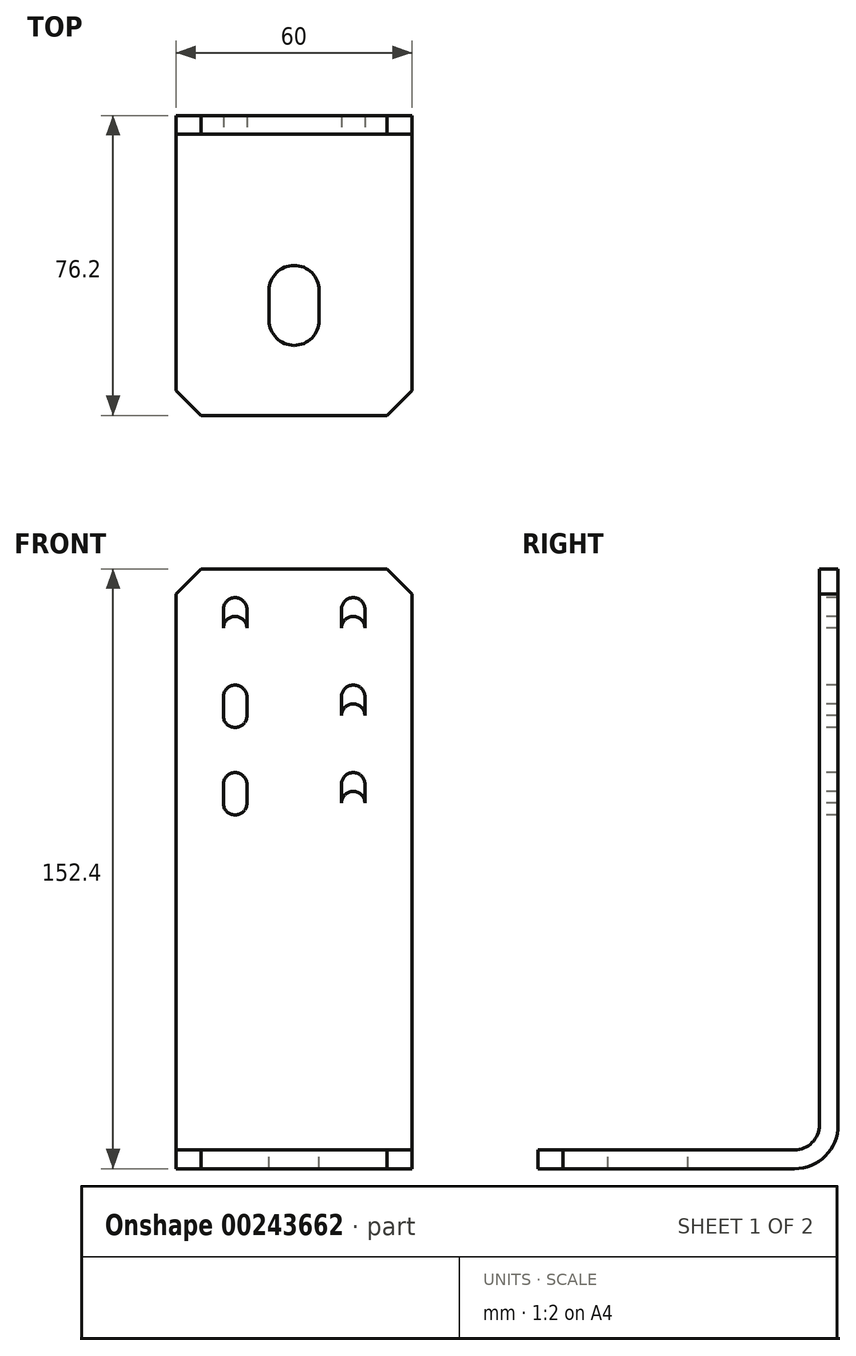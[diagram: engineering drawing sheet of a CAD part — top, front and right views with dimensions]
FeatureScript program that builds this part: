
annotation { "Feature Type Name" : "Feature", "Feature Type Description" : "" }
export const myFeature = defineFeature(function(context is Context, id is Id, definition is map)
    precondition{}
    {
        {
            var Q0;
            Q0=qCreatedBy(makeId("Right.planeOp"),FACE);
            var sketch = newSketch(context, id + "F0", { "sketchPlane" : qUnion([Q0])});
            skLineSegment(sketch, "E0", {"start": v(0, 0) * mm, "end": v(0, 150.02) * mm, "construction": true});
            skLineSegment(sketch, "E1", {"start": v(0, 0) * mm, "end": v(-73.82, 0) * mm, "construction": true});
            skLineSegment(sketch, "E2", {"start": v(-73.82, 2.38) * mm, "end": v(-73.82, -2.38) * mm});
            skLineSegment(sketch, "E3", {"start": v(-73.82, -2.38) * mm, "end": v(2.38, -2.38) * mm});
            skLineSegment(sketch, "E4", {"start": v(2.38, -2.38) * mm, "end": v(2.38, 150.02) * mm});
            skLineSegment(sketch, "E5", {"start": v(2.38, 150.02) * mm, "end": v(-2.38, 150.02) * mm});
            skLineSegment(sketch, "E6", {"start": v(-2.38, 150.02) * mm, "end": v(-2.38, 2.38) * mm});
            skLineSegment(sketch, "E7", {"start": v(-2.38, 2.38) * mm, "end": v(-73.82, 2.38) * mm});
            skSolve(sketch);
        }
        {
            var Q0;
            Q0 = qSketchRegion(id + "F0", true);
            extrude(context, id + "F1", {"entities" : qUnion([Q0]), "endBound" : BoundingType.SYMMETRIC, "depth" : 60 * mm});
        }
        {
            var Q0;
            Q0=makeQuery(id+"F1.opExtrude","SWEPT_EDGE",EDGE,{"disambiguationData":[OSD([sQuery(id+"F0.wireOp",EDGE,"E6"),sQuery(id+"F0.wireOp",EDGE,"E7")])]});
            fillet(context, id + "F2", {"entities" : qUnion([Q0]), "radius" : 6.35 * mm, "tangentPropagation" : true, "allowEdgeOverflow" : false});
        }
        {
            var Q0;
            Q0=makeQuery(id+"F1.opExtrude","SWEPT_EDGE",EDGE,{"disambiguationData":[OSD([sQuery(id+"F0.wireOp",EDGE,"E3"),sQuery(id+"F0.wireOp",EDGE,"E4")])]});
            fillet(context, id + "F3", {"entities" : qUnion([Q0]), "radius" : 11.1 * mm, "tangentPropagation" : true, "allowEdgeOverflow" : false});
        }
        {
            var Q0;
            Q0=makeQuery(id+"F1.opExtrude","CAP_EDGE",EDGE,{"disambiguationData":[OSD([sQuery(id+"F0.wireOp",EDGE,"E5")])],"isStart":false});
            var Q1;
            Q1=makeQuery(id+"F1.opExtrude","CAP_EDGE",EDGE,{"disambiguationData":[OSD([sQuery(id+"F0.wireOp",EDGE,"E5")])],"isStart":true});
            var Q2;
            Q2=makeQuery(id+"F1.opExtrude","CAP_EDGE",EDGE,{"disambiguationData":[OSD([sQuery(id+"F0.wireOp",EDGE,"E2")])],"isStart":true});
            var Q3;
            Q3=makeQuery(id+"F1.opExtrude","CAP_EDGE",EDGE,{"disambiguationData":[OSD([sQuery(id+"F0.wireOp",EDGE,"E2")])],"isStart":false});
            chamfer(context, id + "F4", {"entities" : qUnion([Q0, Q1, Q2, Q3]), "width" : 6.35 * mm, "tangentPropagation" : true});
        }
        {
            var Q0;
            Q0=makeQuery(id+"F1.opExtrude","SWEPT_FACE",FACE,{"disambiguationData":[OSD([sQuery(id+"F0.wireOp",EDGE,"E7")])]});
            var sketch = newSketch(context, id + "F5", { "sketchPlane" : qUnion([Q0])});
            skLineSegment(sketch, "E8", {"start": v(0, 2.38) * mm, "end": v(0, -42.07) * mm, "construction": true});
            skCircle(sketch, "E9", {"center": v(0, -42.07) * mm, "radius": 6.35 * mm});
            skCircle(sketch, "E10", {"center": v(0, -49.69) * mm, "radius": 6.35 * mm});
            skLineSegment(sketch, "E11", {"start": v(0, -42.07) * mm, "end": v(0, -49.69) * mm, "construction": true});
            skLineSegment(sketch, "E12", {"start": v(6.35, -42.07) * mm, "end": v(6.35, -49.69) * mm});
            skLineSegment(sketch, "E13", {"start": v(-6.35, -42.07) * mm, "end": v(-6.35, -49.69) * mm});
            skSolve(sketch);
        }
        {
            var Q0;
            Q0 = qSketchRegion(id + "F5", true);
            extrude(context, id + "F6", {"entities" : qUnion([Q0]), "operationType" : NewBodyOperationType.REMOVE, "endBound" : BoundingType.THROUGH_ALL, "oppositeDirection" : true, "depth" : 25.4 * mm});
        }
        {
            var Q0;
            Q0 = qSketchRegion(id + "F5", true);
            var Q1;
            {var subQ0=sQuery(id+"F5.wireOp",EDGE,"E10");var subQ1=sQuery(id+"F5.wireOp",EDGE,"E9");var subQ2=makeQuery(id+"F5.imprint","INTERSECT",VERTEX,{"disambiguationData":[OD(0.0)],"derivedFrom":[subQ1,subQ0]});Q1=makeQuery(id+"F6.boolean.opBoolean","SPLIT",FACE,{"disambiguationData":[TD([makeQuery(id+"F6.opExtrude","SWEPT_FACE",FACE,{"disambiguationData":[OSD([subQ1]),TDD([makeQuery(id+"F5.imprint","IMPRINT",EDGE,{"disambiguationData":[TD([[subQ2,-1.0]])],"derivedFrom":subQ1})])]})])],"derivedFrom":makeQuery(id+"F1.opExtrude","SWEPT_FACE",FACE,{"disambiguationData":[OSD([sQuery(id+"F0.wireOp",EDGE,"E7")])]})});}
            extrude(context, id + "F7", {"entities" : qUnion([Q0, Q1]), "operationType" : NewBodyOperationType.REMOVE, "endBound" : BoundingType.THROUGH_ALL, "oppositeDirection" : true, "depth" : 25.4 * mm});
        }
        {
            var Q0;
            Q0=makeQuery(id+"F1.opExtrude","SWEPT_FACE",FACE,{"disambiguationData":[OSD([sQuery(id+"F0.wireOp",EDGE,"E6")])]});
            var sketch = newSketch(context, id + "F8", { "sketchPlane" : qUnion([Q0])});
            skLineSegment(sketch, "E14", {"start": v(0, 0) * mm, "end": v(0, 150.02) * mm, "construction": true});
            skCircle(sketch, "E15", {"center": v(-15, 139.7) * mm, "radius": 3 * mm});
            skLineSegment(sketch, "E16", {"start": v(-15, 139.7) * mm, "end": v(-15, 134.94) * mm, "construction": true});
            skCircle(sketch, "E17", {"center": v(-15, 134.94) * mm, "radius": 3 * mm});
            skLineSegment(sketch, "E18", {"start": v(-12, 139.7) * mm, "end": v(-12, 134.94) * mm});
            skLineSegment(sketch, "E19", {"start": v(-18, 139.7) * mm, "end": v(-18, 134.94) * mm});
            skLineSegment(sketch, "E20", {"start": v(-18, 137.32) * mm, "end": v(-12, 137.32) * mm, "construction": true});
            skCircle(sketch, "E21.0.1.0", {"center": v(-15, 112.71) * mm, "radius": 3 * mm});
            skLineSegment(sketch, "E21.0.1.1", {"start": v(-15, 117.48) * mm, "end": v(-15, 112.71) * mm, "construction": true});
            skLineSegment(sketch, "E21.0.1.2", {"start": v(-12, 117.48) * mm, "end": v(-12, 112.71) * mm});
            skLineSegment(sketch, "E21.0.1.3", {"start": v(-18, 117.48) * mm, "end": v(-18, 112.71) * mm});
            skLineSegment(sketch, "E21.0.1.4", {"start": v(-18, 115.1) * mm, "end": v(-12, 115.1) * mm, "construction": true});
            skCircle(sketch, "E21.0.1.5", {"center": v(-15, 117.48) * mm, "radius": 3 * mm});
            skCircle(sketch, "E21.0.2.0", {"center": v(-15, 90.49) * mm, "radius": 3 * mm});
            skLineSegment(sketch, "E21.0.2.1", {"start": v(-15, 95.25) * mm, "end": v(-15, 90.49) * mm, "construction": true});
            skLineSegment(sketch, "E21.0.2.2", {"start": v(-12, 95.25) * mm, "end": v(-12, 90.49) * mm});
            skLineSegment(sketch, "E21.0.2.3", {"start": v(-18, 95.25) * mm, "end": v(-18, 90.49) * mm});
            skLineSegment(sketch, "E21.0.2.4", {"start": v(-18, 92.87) * mm, "end": v(-12, 92.87) * mm, "construction": true});
            skCircle(sketch, "E21.0.2.5", {"center": v(-15, 95.25) * mm, "radius": 3 * mm});
            skLineSegment(sketch, "E21.direction1", {"start": v(-18, 134.94) * mm, "end": v(7.6, 134.94) * mm, "construction": true});
            skLineSegment(sketch, "E21.direction2", {"start": v(-18, 134.94) * mm, "end": v(-18, 112.71) * mm, "construction": true});
            skLineSegment(sketch, "E22.MirrorCS", {"start": v(15, 139.7) * mm, "end": v(15, 134.94) * mm, "construction": true});
            skLineSegment(sketch, "E23.MirrorCS", {"start": v(15, 117.48) * mm, "end": v(15, 112.71) * mm, "construction": true});
            skLineSegment(sketch, "E24.MirrorCS", {"start": v(12, 95.25) * mm, "end": v(12, 90.49) * mm});
            skLineSegment(sketch, "E25.MirrorCS", {"start": v(18, 95.25) * mm, "end": v(18, 90.49) * mm});
            skLineSegment(sketch, "E26.MirrorCS", {"start": v(18, 92.87) * mm, "end": v(12, 92.87) * mm, "construction": true});
            skLineSegment(sketch, "E27.MirrorCS", {"start": v(18, 115.1) * mm, "end": v(12, 115.1) * mm, "construction": true});
            skLineSegment(sketch, "E28.MirrorCS", {"start": v(18, 117.48) * mm, "end": v(18, 112.71) * mm});
            skLineSegment(sketch, "E29.MirrorCS", {"start": v(12, 139.7) * mm, "end": v(12, 134.94) * mm});
            skLineSegment(sketch, "E30.MirrorCS", {"start": v(18, 139.7) * mm, "end": v(18, 134.94) * mm});
            skLineSegment(sketch, "E31.MirrorCS", {"start": v(18, 137.32) * mm, "end": v(12, 137.32) * mm, "construction": true});
            skLineSegment(sketch, "E32.MirrorCS", {"start": v(12, 117.48) * mm, "end": v(12, 112.71) * mm});
            skCircle(sketch, "E33.MirrorC", {"center": v(15, 139.7) * mm, "radius": 3 * mm});
            skCircle(sketch, "E34.MirrorC", {"center": v(15, 95.25) * mm, "radius": 3 * mm});
            skLineSegment(sketch, "E35.MirrorCS", {"start": v(15, 95.25) * mm, "end": v(15, 90.49) * mm, "construction": true});
            skLineSegment(sketch, "E36.MirrorCS", {"start": v(18, 134.94) * mm, "end": v(18, 112.71) * mm, "construction": true});
            skCircle(sketch, "E37.MirrorC", {"center": v(15, 90.49) * mm, "radius": 3 * mm});
            skCircle(sketch, "E38.MirrorC", {"center": v(15, 117.48) * mm, "radius": 3 * mm});
            skCircle(sketch, "E39.MirrorC", {"center": v(15, 134.94) * mm, "radius": 3 * mm});
            skCircle(sketch, "E40.MirrorC", {"center": v(15, 112.71) * mm, "radius": 3 * mm});
            skSolve(sketch);
        }
        {
            var Q0;
            {var subQ0=sQuery(id+"F8.wireOp",EDGE,"E19");Q0=makeQuery(id+"F8.imprint","IMPRINT",FACE,{"disambiguationData":[TD([[makeQuery(id+"F8.imprint","IMPRINT",EDGE,{"derivedFrom":subQ0}),1.0]])]});}
            var Q1;
            {var subQ0=sQuery(id+"F8.wireOp",EDGE,"E18");Q1=makeQuery(id+"F8.imprint","IMPRINT",FACE,{"disambiguationData":[TD([[makeQuery(id+"F8.imprint","IMPRINT",EDGE,{"derivedFrom":subQ0}),-1.0]])]});}
            var Q2;
            {var subQ0=sQuery(id+"F8.wireOp",EDGE,"E21.0.1.2");Q2=makeQuery(id+"F8.imprint","IMPRINT",FACE,{"disambiguationData":[TD([[makeQuery(id+"F8.imprint","IMPRINT",EDGE,{"derivedFrom":subQ0}),-1.0]])]});}
            var Q3;
            {var subQ0=sQuery(id+"F8.wireOp",EDGE,"E21.0.1.3");Q3=makeQuery(id+"F8.imprint","IMPRINT",FACE,{"disambiguationData":[TD([[makeQuery(id+"F8.imprint","IMPRINT",EDGE,{"derivedFrom":subQ0}),1.0]])]});}
            var Q4;
            {var subQ0=sQuery(id+"F8.wireOp",EDGE,"E21.0.2.2");Q4=makeQuery(id+"F8.imprint","IMPRINT",FACE,{"disambiguationData":[TD([[makeQuery(id+"F8.imprint","IMPRINT",EDGE,{"derivedFrom":subQ0}),-1.0]])]});}
            var Q5;
            {var subQ0=sQuery(id+"F8.wireOp",EDGE,"E21.0.2.3");Q5=makeQuery(id+"F8.imprint","IMPRINT",FACE,{"disambiguationData":[TD([[makeQuery(id+"F8.imprint","IMPRINT",EDGE,{"derivedFrom":subQ0}),1.0]])]});}
            var Q6;
            {var subQ0=sQuery(id+"F8.wireOp",EDGE,"E24.MirrorCS");Q6=makeQuery(id+"F8.imprint","IMPRINT",FACE,{"disambiguationData":[TD([[makeQuery(id+"F8.imprint","IMPRINT",EDGE,{"derivedFrom":subQ0}),1.0]])]});}
            var Q7;
            {var subQ0=sQuery(id+"F8.wireOp",EDGE,"E25.MirrorCS");Q7=makeQuery(id+"F8.imprint","IMPRINT",FACE,{"disambiguationData":[TD([[makeQuery(id+"F8.imprint","IMPRINT",EDGE,{"derivedFrom":subQ0}),-1.0]])]});}
            var Q8;
            {var subQ0=sQuery(id+"F8.wireOp",EDGE,"E28.MirrorCS");Q8=makeQuery(id+"F8.imprint","IMPRINT",FACE,{"disambiguationData":[TD([[makeQuery(id+"F8.imprint","IMPRINT",EDGE,{"derivedFrom":subQ0}),-1.0]])]});}
            var Q9;
            {var subQ0=sQuery(id+"F8.wireOp",EDGE,"E29.MirrorCS");Q9=makeQuery(id+"F8.imprint","IMPRINT",FACE,{"disambiguationData":[TD([[makeQuery(id+"F8.imprint","IMPRINT",EDGE,{"derivedFrom":subQ0}),1.0]])]});}
            var Q10;
            {var subQ0=sQuery(id+"F8.wireOp",EDGE,"E30.MirrorCS");Q10=makeQuery(id+"F8.imprint","IMPRINT",FACE,{"disambiguationData":[TD([[makeQuery(id+"F8.imprint","IMPRINT",EDGE,{"derivedFrom":subQ0}),-1.0]])]});}
            var Q11;
            {var subQ0=sQuery(id+"F8.wireOp",EDGE,"E32.MirrorCS");Q11=makeQuery(id+"F8.imprint","IMPRINT",FACE,{"disambiguationData":[TD([[makeQuery(id+"F8.imprint","IMPRINT",EDGE,{"derivedFrom":subQ0}),1.0]])]});}
            var Q12;
            {var subQ0=sQuery(id+"F8.wireOp",EDGE,"E17");var subQ1=sQuery(id+"F8.wireOp",EDGE,"E15");var subQ2=makeQuery(id+"F8.imprint","INTERSECT",VERTEX,{"disambiguationData":[OD(0.0)],"derivedFrom":[subQ1,subQ0]});Q12=makeQuery(id+"F8.imprint","IMPRINT",FACE,{"disambiguationData":[TD([[makeQuery(id+"F8.imprint","IMPRINT",EDGE,{"disambiguationData":[TD([[subQ2,-1.0]])],"derivedFrom":subQ1}),-1.0]])]});}
            var Q13;
            {var subQ0=sQuery(id+"F8.wireOp",EDGE,"E21.0.1.0");var subQ1=makeQuery(id+"F8.imprint","INTERSECT",VERTEX,{"derivedFrom":[subQ0,sQuery(id+"F8.wireOp",EDGE,"E21.0.1.2")]});Q13=makeQuery(id+"F8.imprint","IMPRINT",FACE,{"disambiguationData":[TD([[makeQuery(id+"F8.imprint","IMPRINT",EDGE,{"disambiguationData":[TD([[subQ1,-1.0]])],"derivedFrom":subQ0}),1.0]])]});}
            var Q14;
            {var subQ0=sQuery(id+"F8.wireOp",EDGE,"E21.0.1.5");var subQ1=sQuery(id+"F8.wireOp",EDGE,"E21.0.1.0");var subQ2=makeQuery(id+"F8.imprint","INTERSECT",VERTEX,{"disambiguationData":[OD(0.0)],"derivedFrom":[subQ1,subQ0]});Q14=makeQuery(id+"F8.imprint","IMPRINT",FACE,{"disambiguationData":[TD([[makeQuery(id+"F8.imprint","IMPRINT",EDGE,{"disambiguationData":[TD([[subQ2,-1.0]])],"derivedFrom":subQ1}),-1.0]])]});}
            var Q15;
            {var subQ0=sQuery(id+"F8.wireOp",EDGE,"E21.0.2.0");var subQ1=makeQuery(id+"F8.imprint","INTERSECT",VERTEX,{"derivedFrom":[subQ0,sQuery(id+"F8.wireOp",EDGE,"E21.0.2.2")]});Q15=makeQuery(id+"F8.imprint","IMPRINT",FACE,{"disambiguationData":[TD([[makeQuery(id+"F8.imprint","IMPRINT",EDGE,{"disambiguationData":[TD([[subQ1,-1.0]])],"derivedFrom":subQ0}),1.0]])]});}
            var Q16;
            {var subQ0=sQuery(id+"F8.wireOp",EDGE,"E21.0.2.5");var subQ1=sQuery(id+"F8.wireOp",EDGE,"E21.0.2.0");var subQ2=makeQuery(id+"F8.imprint","INTERSECT",VERTEX,{"disambiguationData":[OD(0.0)],"derivedFrom":[subQ1,subQ0]});Q16=makeQuery(id+"F8.imprint","IMPRINT",FACE,{"disambiguationData":[TD([[makeQuery(id+"F8.imprint","IMPRINT",EDGE,{"disambiguationData":[TD([[subQ2,-1.0]])],"derivedFrom":subQ1}),-1.0]])]});}
            var Q17;
            {var subQ0=sQuery(id+"F8.wireOp",EDGE,"E33.MirrorC");var subQ1=makeQuery(id+"F8.imprint","INTERSECT",VERTEX,{"derivedFrom":[sQuery(id+"F8.wireOp",EDGE,"E29.MirrorCS"),subQ0]});Q17=makeQuery(id+"F8.imprint","IMPRINT",FACE,{"disambiguationData":[TD([[makeQuery(id+"F8.imprint","IMPRINT",EDGE,{"disambiguationData":[TD([[subQ1,-1.0]])],"derivedFrom":subQ0}),-1.0]])]});}
            var Q18;
            {var subQ0=sQuery(id+"F8.wireOp",EDGE,"E39.MirrorC");var subQ1=sQuery(id+"F8.wireOp",EDGE,"E33.MirrorC");var subQ2=makeQuery(id+"F8.imprint","INTERSECT",VERTEX,{"disambiguationData":[OD(0.0)],"derivedFrom":[subQ1,subQ0]});Q18=makeQuery(id+"F8.imprint","IMPRINT",FACE,{"disambiguationData":[TD([[makeQuery(id+"F8.imprint","IMPRINT",EDGE,{"disambiguationData":[TD([[subQ2,-1.0]])],"derivedFrom":subQ1}),1.0]])]});}
            var Q19;
            {var subQ0=sQuery(id+"F8.wireOp",EDGE,"E34.MirrorC");var subQ1=makeQuery(id+"F8.imprint","INTERSECT",VERTEX,{"derivedFrom":[sQuery(id+"F8.wireOp",EDGE,"E24.MirrorCS"),subQ0]});Q19=makeQuery(id+"F8.imprint","IMPRINT",FACE,{"disambiguationData":[TD([[makeQuery(id+"F8.imprint","IMPRINT",EDGE,{"disambiguationData":[TD([[subQ1,-1.0]])],"derivedFrom":subQ0}),-1.0]])]});}
            var Q20;
            {var subQ0=sQuery(id+"F8.wireOp",EDGE,"E37.MirrorC");var subQ1=sQuery(id+"F8.wireOp",EDGE,"E34.MirrorC");var subQ2=makeQuery(id+"F8.imprint","INTERSECT",VERTEX,{"disambiguationData":[OD(0.0)],"derivedFrom":[subQ1,subQ0]});Q20=makeQuery(id+"F8.imprint","IMPRINT",FACE,{"disambiguationData":[TD([[makeQuery(id+"F8.imprint","IMPRINT",EDGE,{"disambiguationData":[TD([[subQ2,-1.0]])],"derivedFrom":subQ1}),1.0]])]});}
            var Q21;
            {var subQ0=sQuery(id+"F8.wireOp",EDGE,"E38.MirrorC");var subQ1=makeQuery(id+"F8.imprint","INTERSECT",VERTEX,{"derivedFrom":[sQuery(id+"F8.wireOp",EDGE,"E28.MirrorCS"),subQ0]});Q21=makeQuery(id+"F8.imprint","IMPRINT",FACE,{"disambiguationData":[TD([[makeQuery(id+"F8.imprint","IMPRINT",EDGE,{"disambiguationData":[TD([[subQ1,1.0]])],"derivedFrom":subQ0}),-1.0]])]});}
            var Q22;
            {var subQ0=sQuery(id+"F8.wireOp",EDGE,"E40.MirrorC");var subQ1=sQuery(id+"F8.wireOp",EDGE,"E38.MirrorC");var subQ2=makeQuery(id+"F8.imprint","INTERSECT",VERTEX,{"disambiguationData":[OD(0.0)],"derivedFrom":[subQ1,subQ0]});Q22=makeQuery(id+"F8.imprint","IMPRINT",FACE,{"disambiguationData":[TD([[makeQuery(id+"F8.imprint","IMPRINT",EDGE,{"disambiguationData":[TD([[subQ2,-1.0]])],"derivedFrom":subQ1}),1.0]])]});}
            var Q23;
            {var subQ0=sQuery(id+"F8.wireOp",EDGE,"E17");var subQ1=sQuery(id+"F8.wireOp",EDGE,"E15");var subQ2=makeQuery(id+"F8.imprint","INTERSECT",VERTEX,{"disambiguationData":[OD(0.0)],"derivedFrom":[subQ1,subQ0]});Q23=makeQuery(id+"F8.imprint","IMPRINT",FACE,{"disambiguationData":[TD([[makeQuery(id+"F8.imprint","IMPRINT",EDGE,{"disambiguationData":[TD([[subQ2,-1.0]])],"derivedFrom":subQ1}),1.0]])]});}
            var Q24;
            {var subQ0=sQuery(id+"F8.wireOp",EDGE,"E15");var subQ1=makeQuery(id+"F8.imprint","INTERSECT",VERTEX,{"derivedFrom":[subQ0,sQuery(id+"F8.wireOp",EDGE,"E18")]});Q24=makeQuery(id+"F8.imprint","IMPRINT",FACE,{"disambiguationData":[TD([[makeQuery(id+"F8.imprint","IMPRINT",EDGE,{"disambiguationData":[TD([[subQ1,-1.0]])],"derivedFrom":subQ0}),1.0]])]});}
            var Q25;
            {var subQ0=sQuery(id+"F8.wireOp",EDGE,"E21.0.1.5");var subQ1=sQuery(id+"F8.wireOp",EDGE,"E21.0.1.0");var subQ2=makeQuery(id+"F8.imprint","INTERSECT",VERTEX,{"disambiguationData":[OD(0.0)],"derivedFrom":[subQ1,subQ0]});Q25=makeQuery(id+"F8.imprint","IMPRINT",FACE,{"disambiguationData":[TD([[makeQuery(id+"F8.imprint","IMPRINT",EDGE,{"disambiguationData":[TD([[subQ2,-1.0]])],"derivedFrom":subQ1}),1.0]])]});}
            var Q26;
            {var subQ0=sQuery(id+"F8.wireOp",EDGE,"E39.MirrorC");var subQ1=sQuery(id+"F8.wireOp",EDGE,"E33.MirrorC");var subQ2=makeQuery(id+"F8.imprint","INTERSECT",VERTEX,{"disambiguationData":[OD(0.0)],"derivedFrom":[subQ1,subQ0]});Q26=makeQuery(id+"F8.imprint","IMPRINT",FACE,{"disambiguationData":[TD([[makeQuery(id+"F8.imprint","IMPRINT",EDGE,{"disambiguationData":[TD([[subQ2,-1.0]])],"derivedFrom":subQ1}),-1.0]])]});}
            var Q27;
            {var subQ0=sQuery(id+"F8.wireOp",EDGE,"E40.MirrorC");var subQ1=sQuery(id+"F8.wireOp",EDGE,"E38.MirrorC");var subQ2=makeQuery(id+"F8.imprint","INTERSECT",VERTEX,{"disambiguationData":[OD(0.0)],"derivedFrom":[subQ1,subQ0]});Q27=makeQuery(id+"F8.imprint","IMPRINT",FACE,{"disambiguationData":[TD([[makeQuery(id+"F8.imprint","IMPRINT",EDGE,{"disambiguationData":[TD([[subQ2,-1.0]])],"derivedFrom":subQ1}),-1.0]])]});}
            var Q28;
            {var subQ0=sQuery(id+"F8.wireOp",EDGE,"E37.MirrorC");var subQ1=sQuery(id+"F8.wireOp",EDGE,"E34.MirrorC");var subQ2=makeQuery(id+"F8.imprint","INTERSECT",VERTEX,{"disambiguationData":[OD(0.0)],"derivedFrom":[subQ1,subQ0]});Q28=makeQuery(id+"F8.imprint","IMPRINT",FACE,{"disambiguationData":[TD([[makeQuery(id+"F8.imprint","IMPRINT",EDGE,{"disambiguationData":[TD([[subQ2,-1.0]])],"derivedFrom":subQ1}),-1.0]])]});}
            var Q29;
            {var subQ0=sQuery(id+"F8.wireOp",EDGE,"E21.0.2.5");var subQ1=sQuery(id+"F8.wireOp",EDGE,"E21.0.2.0");var subQ2=makeQuery(id+"F8.imprint","INTERSECT",VERTEX,{"disambiguationData":[OD(0.0)],"derivedFrom":[subQ1,subQ0]});Q29=makeQuery(id+"F8.imprint","IMPRINT",FACE,{"disambiguationData":[TD([[makeQuery(id+"F8.imprint","IMPRINT",EDGE,{"disambiguationData":[TD([[subQ2,-1.0]])],"derivedFrom":subQ1}),1.0]])]});}
            extrude(context, id + "F9", {"entities" : qUnion([Q0, Q1, Q2, Q3, Q4, Q5, Q6, Q7, Q8, Q9, Q10, Q11, Q12, Q13, Q14, Q15, Q16, Q17, Q18, Q19, Q20, Q21, Q22, Q23, Q24, Q25, Q26, Q27, Q28, Q29]), "operationType" : NewBodyOperationType.REMOVE, "endBound" : BoundingType.THROUGH_ALL, "oppositeDirection" : true, "depth" : 25.4 * mm});
        }
    });
